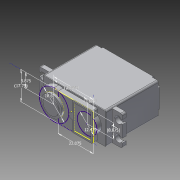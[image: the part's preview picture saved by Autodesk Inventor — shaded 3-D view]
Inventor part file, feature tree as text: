
AUTODESK INVENTOR PART (.ipt)
format: ipt  version: 2015 (Build 190159000, 159)  size: 269,824 bytes
history: native  units: in
note: dims shown in document units (in); Inventor stores cm internally (conversion verified against a paired STEP export)
features: projected_geometry x4, other x3, direct_edit x1, sketch x1, imported_body x1
ambient origin geometry x8: Origin, YZ Plane, XZ Plane, XY Plane, X Axis, Y Axis, Z Axis, Center Point
bodies: Solid1 (feature_tree)
feature tree (10):
  other  "SW3dPS-Hitec Servo.SAT1"
  other  "Move Face1"
  direct_edit  "Direct Edit1"
  sketch  "Sketch1"  dims[d0=0.7323in d1=0.9785in d2=0.3494in d3=0.4893in d4=0.3494in d5=0.1517in d6=0.8268in d7=0.6988in d8=0.8691in d9=0.3939in]
  imported_body  "Base1"
  projected_geometry  "Projected Loop1"
  projected_geometry  "Projected Loop2"
  projected_geometry  "Projected Loop3"
  projected_geometry  "Projected Loop4"
  other  "Delete1"
